# Revit family: LTV8RG
name_source: partatom
category: Lighting Fixtures
units: mm (PartAtom-declared; Revit-internal decimal feet)

## family parameters
Cut with Voids When Loaded = No
Host = Face
Light Source = Yes
OmniClass Number = 23.80.70.14.17
OmniClass Title = Exterior Spotlights
Part Type = Normal
Room Calculation Point = No
Round Connector Dimension = Use Diameter
Shared = No

## types (2) — shared parameters
Apparent Load = 0 VA
Certification = ■ UL 1598 Standard for Luminaires.
■ UL 8750 Standard for Safety for Light
Emitting Diode (LED) Equipment for use
in Lighting Products.
Color Filter = 16777215
Default Elevation = 48.000"
Description = Sealed Light Engine with Bluetooth® Connectivity
Dimming Lamp Color Temperature Shift = <None>
Emit Shape Visible in Rendering = No
Features = ■ Bluetooth connectivity for remote control
aiming, dimming, color changing
■ Hardwired DMX connectivity for advanced
control (controller supplied by others)
■ Free mobile App for Adroid and iOS
■ IP68 sealed light engine
Guard Finish = Powdercoat - Bronze
Housing Material = Powdercoat - Black
Lens = White Glass
Load Classification = Lighting
Manufacturer = Kim Lighting
Model = Lightvault® LTV8DM Directional Marker
Photometric Notes = More IES files download on Photometric Web Link
Power Factor = 1
Tilt Angle = 90.00°
URL = https://www.currentlighting.com
Voltage = 120 V
Warranty = 5 Years Limited Warranty
Wattage Comments = 14W, 23W & 44W

## per-type parameters (varying)
| type | Diameter | Emit from Circle Diameter | Height | Lamp | Photometric Web File | Radius |
| LTV82RG | 10.375" | 9.375" | 9.875" | 18 LEDs | ltv82rg-nf-18l4k.ies | 5.188" |
| LTV81RG | 13.000" | 12.000" | 10.000" | 36 LEDs | ltv81rg-sp-36l3k.ies | 6.500" |

note: column(s) folded — value = type name in every type: Cover

## geometry (parser evidence)
native form markers: Blend x3, Sweep x8
no freeform markers — native parametric forms only
